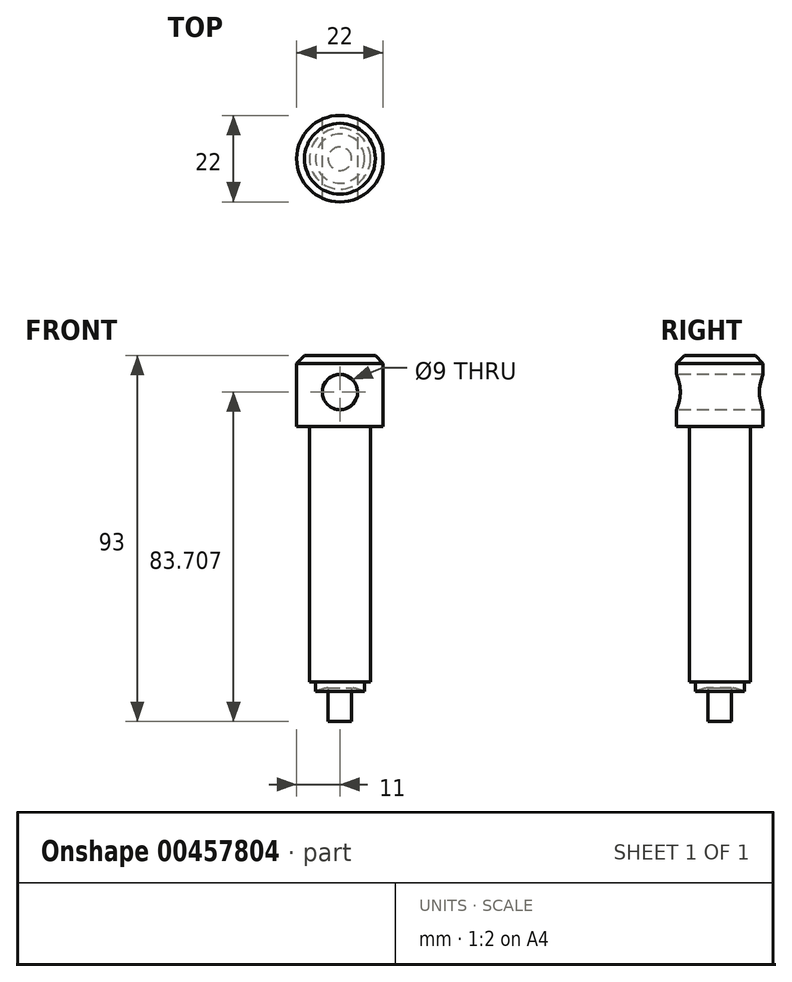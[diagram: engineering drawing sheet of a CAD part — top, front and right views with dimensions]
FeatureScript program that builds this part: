
annotation { "Feature Type Name" : "Feature", "Feature Type Description" : "" }
export const myFeature = defineFeature(function(context is Context, id is Id, definition is map)
    precondition{}
    {
        {
            var Q0;
            Q0=qCreatedBy(makeId("Front.planeOp"),FACE);
            var sketch = newSketch(context, id + "F0", { "sketchPlane" : qUnion([Q0])});
            skLineSegment(sketch, "E0", {"start": v(0, -22.96) * mm, "end": v(0, 110.83) * mm, "construction": true});
            skLineSegment(sketch, "E1", {"start": v(-9, 93) * mm, "end": v(0, 93) * mm});
            skLineSegment(sketch, "E2", {"start": v(-9, 93) * mm, "end": v(-11, 91) * mm});
            skLineSegment(sketch, "E3", {"start": v(-11, 91) * mm, "end": v(-11, 75) * mm});
            skLineSegment(sketch, "E4", {"start": v(-11, 75) * mm, "end": v(-7.75, 75) * mm});
            skLineSegment(sketch, "E5", {"start": v(-7.75, 75) * mm, "end": v(-7.75, 10) * mm});
            skLineSegment(sketch, "E6", {"start": v(-7.75, 10) * mm, "end": v(-6.25, 10) * mm});
            skLineSegment(sketch, "E7", {"start": v(-6.25, 10) * mm, "end": v(-6.25, 7.65) * mm});
            skLineSegment(sketch, "E8", {"start": v(-3, 8.57) * mm, "end": v(-3, 0) * mm});
            skLineSegment(sketch, "E9", {"start": v(-3, 0) * mm, "end": v(0, 0) * mm});
            skLineSegment(sketch, "E10", {"start": v(-7.75, 73) * mm, "end": v(0, 73) * mm, "construction": true});
            skArc(sketch, "E11", {"start": v(-3, 8.57) * mm, "mid": v(-4.65, 8.2) * mm, "end": v(-6.25, 7.65) * mm});
            skLineSegment(sketch, "E12", {"start": v(0, 93) * mm, "end": v(0, 0) * mm});
            skSolve(sketch);
        }
        {
            var Q0;
            Q0=makeQuery(id+"F0.imprint","IMPRINT",FACE,{"disambiguationData":[TD([[makeQuery(id+"F0.imprint","IMPRINT",EDGE,{"derivedFrom":sQuery(id+"F0.wireOp",EDGE,"E1")}),-1.0]])]});
            var Q1;
            Q1=sQuery(id+"F0.wireOp",EDGE,"E0");
            revolve(context, id + "F1", {"entities" : qUnion([Q0]), "axis" : qUnion([Q1]), "revolveType" : RevolveType.FULL});
        }
        {
            var Q0;
            Q0=qCreatedBy(makeId("Front.planeOp"),FACE);
            var sketch = newSketch(context, id + "F2", { "sketchPlane" : qUnion([Q0])});
            skCircle(sketch, "E13", {"center": v(0, 83.7) * mm, "radius": 4.5 * mm});
            skSolve(sketch);
        }
        {
            var Q0;
            Q0 = qSketchRegion(id + "F2", true);
            extrude(context, id + "F3", {"entities" : qUnion([Q0]), "operationType" : NewBodyOperationType.REMOVE, "endBound" : BoundingType.THROUGH_ALL, "oppositeDirection" : true, "depth" : 25 * mm, "hasSecondDirection" : true, "secondDirectionBound" : BoundingType.THROUGH_ALL, "secondDirectionOppositeDirection" : false, "secondDirectionDepth" : 25 * mm});
        }
    });
